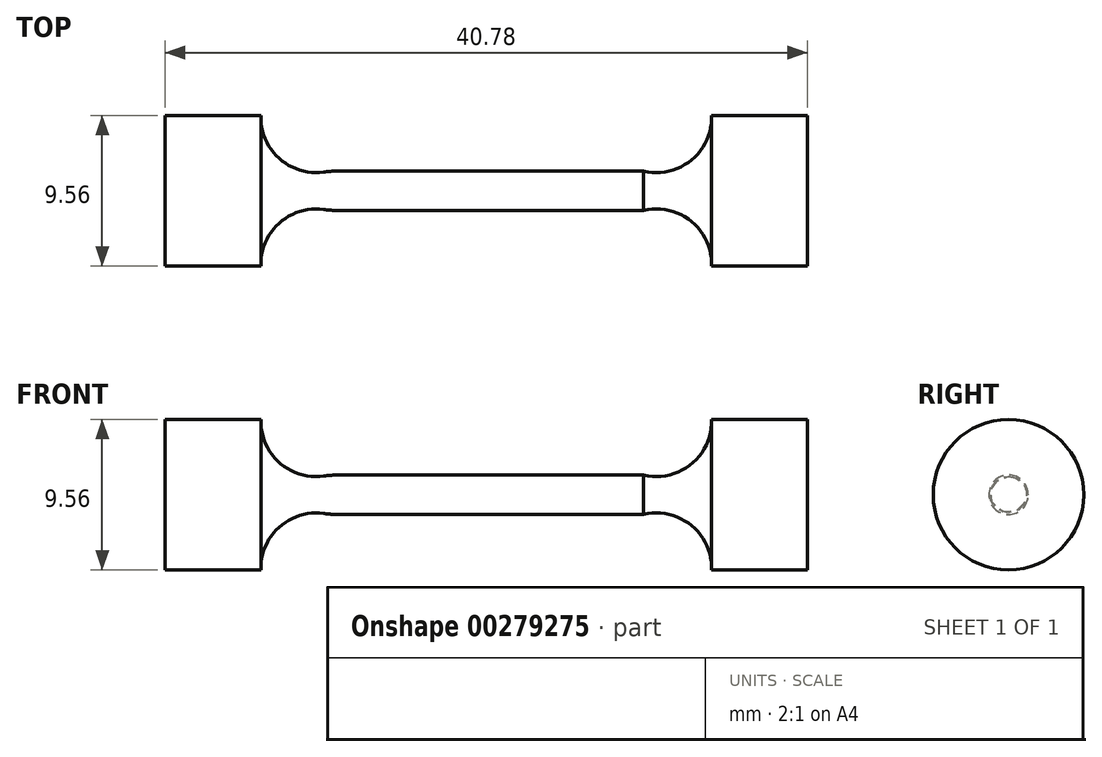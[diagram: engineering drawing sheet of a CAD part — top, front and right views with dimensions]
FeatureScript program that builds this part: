
annotation { "Feature Type Name" : "Feature", "Feature Type Description" : "" }
export const myFeature = defineFeature(function(context is Context, id is Id, definition is map)
    precondition{}
    {
        {
            var Q0;
            Q0=qCreatedBy(makeId("Front.planeOp"),FACE);
            var sketch = newSketch(context, id + "F0", { "sketchPlane" : qUnion([Q0])});
            skLineSegment(sketch, "E0", {"start": v(0, 1.25) * mm, "end": v(10, 1.25) * mm});
            skArc(sketch, "E1", {"start": v(10, 1.25) * mm, "mid": v(13.03, 1.95) * mm, "end": v(14.31, 4.78) * mm});
            skLineSegment(sketch, "E2", {"start": v(14.31, 4.78) * mm, "end": v(20.4, 4.78) * mm});
            skLineSegment(sketch, "E3", {"start": v(20.4, 4.78) * mm, "end": v(20.4, 0) * mm});
            skLineSegment(sketch, "E4", {"start": v(20.4, 0) * mm, "end": v(0, 0) * mm});
            skLineSegment(sketch, "E5.MirrorCS", {"start": v(0, 1.25) * mm, "end": v(-9.45, 1.25) * mm});
            skLineSegment(sketch, "E6.MirrorCS", {"start": v(-20.4, 0) * mm, "end": v(0, 0) * mm});
            skLineSegment(sketch, "E7.MirrorCS", {"start": v(-14.31, 4.78) * mm, "end": v(-20.4, 4.78) * mm});
            skLineSegment(sketch, "E8.MirrorCS", {"start": v(-20.4, 4.78) * mm, "end": v(-20.4, 0) * mm});
            skArc(sketch, "E9.MirrorCS", {"start": v(-10.32, 1.19) * mm, "mid": v(-13.15, 2.06) * mm, "end": v(-14.31, 4.78) * mm});
            skPoint(sketch, "E10.visualSharp", {"position": v(-10, 1.25) * mm});
            skArc(sketch, "E10.filletArc", {"start": v(-9.45, 1.25) * mm, "mid": v(-9.89, 1.23) * mm, "end": v(-10.32, 1.19) * mm});
            skSolve(sketch);
        }
        {
            var Q0;
            Q0=makeQuery(id+"F0.imprint","IMPRINT",FACE,{"disambiguationData":[TD([[makeQuery(id+"F0.imprint","IMPRINT",EDGE,{"derivedFrom":sQuery(id+"F0.wireOp",EDGE,"E0")}),-1.0]])]});
            var Q1;
            Q1=sQuery(id+"F0.wireOp",EDGE,"E6.MirrorCS");
            revolve(context, id + "F1", {"entities" : qUnion([Q0]), "axis" : qUnion([Q1]), "revolveType" : RevolveType.FULL});
        }
    });
